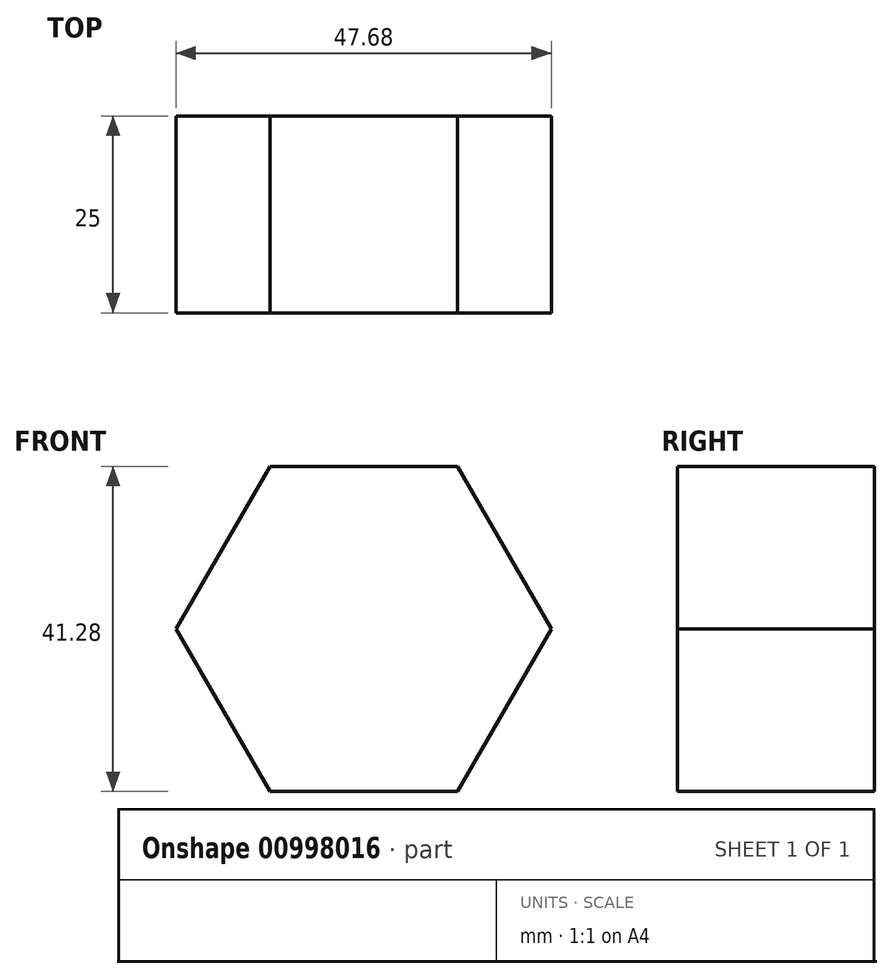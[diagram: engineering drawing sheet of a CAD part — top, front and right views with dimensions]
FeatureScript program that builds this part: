
annotation { "Feature Type Name" : "Feature", "Feature Type Description" : "" }
export const myFeature = defineFeature(function(context is Context, id is Id, definition is map)
    precondition{}
    {
        {
            var Q0;
            Q0=qCreatedBy(makeId("Front.planeOp"),FACE);
            var sketch = newSketch(context, id + "F0", { "sketchPlane" : qUnion([Q0])});
            skCircle(sketch, "E0.cCircle", {"center": v(0, 0) * mm, "radius": 20.64 * mm, "construction": true});
            skLineSegment(sketch, "E0.0", {"start": v(11.92, -20.64) * mm, "end": v(-11.92, -20.64) * mm});
            skLineSegment(sketch, "E0.1", {"start": v(-11.92, -20.64) * mm, "end": v(-23.84, 0) * mm});
            skLineSegment(sketch, "E0.2", {"start": v(-23.84, 0) * mm, "end": v(-11.92, 20.64) * mm});
            skLineSegment(sketch, "E0.3", {"start": v(-11.92, 20.64) * mm, "end": v(11.92, 20.64) * mm});
            skLineSegment(sketch, "E0.4", {"start": v(11.92, 20.64) * mm, "end": v(23.84, 0) * mm});
            skLineSegment(sketch, "E0.5", {"start": v(23.84, 0) * mm, "end": v(11.92, -20.64) * mm});
            skPoint(sketch, "E0.0.midPoint", {"position": v(0, -20.64) * mm});
            skSolve(sketch);
        }
        {
            var Q0;
            Q0=sQuery(id+"F0.wireOp",EDGE,"E0.2");
            var Q1;
            Q1=sQuery(id+"F0.wireOp",EDGE,"E0.3");
            var Q2;
            Q2=sQuery(id+"F0.wireOp",EDGE,"E0.4");
            var Q3;
            Q3=sQuery(id+"F0.wireOp",EDGE,"E0.5");
            var Q4;
            Q4=sQuery(id+"F0.wireOp",EDGE,"E0.0");
            var Q5;
            Q5=sQuery(id+"F0.wireOp",EDGE,"E0.1");
            extrude(context, id + "F1", {"bodyType" : ToolBodyType.SURFACE, "surfaceEntities" : qUnion([Q0, Q1, Q2, Q3, Q4, Q5]), "depth" : 25 * mm, "offsetDistance" : 25 * mm});
        }
    });
